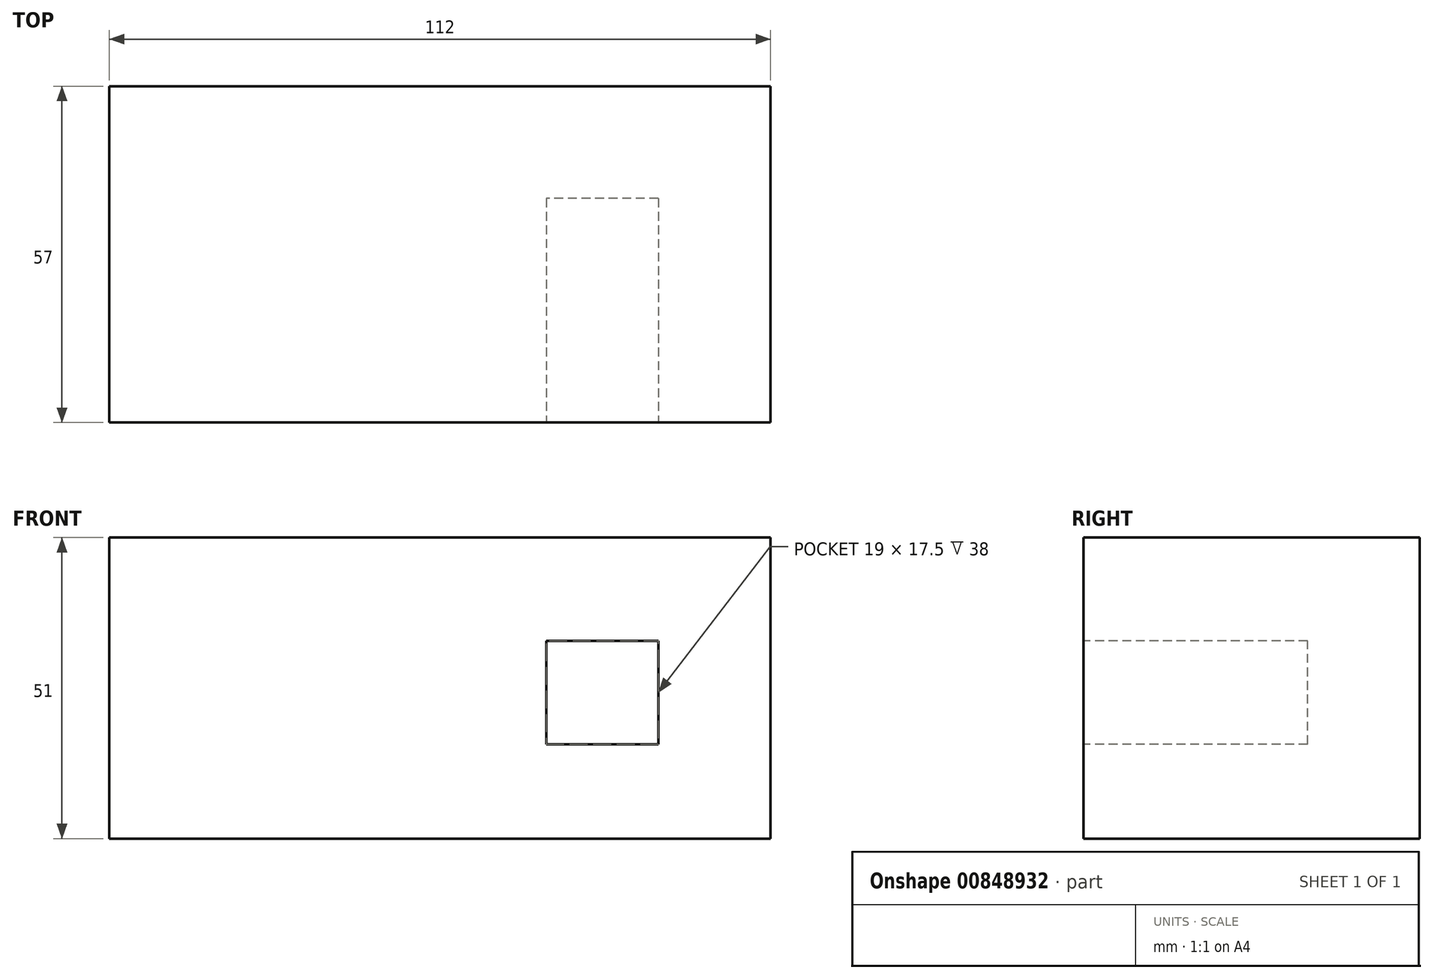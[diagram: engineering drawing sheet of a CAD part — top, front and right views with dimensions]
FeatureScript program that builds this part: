
annotation { "Feature Type Name" : "Feature", "Feature Type Description" : "" }
export const myFeature = defineFeature(function(context is Context, id is Id, definition is map)
    precondition{}
    {
        {
            var Q0;
            Q0=qCreatedBy(makeId("Front.planeOp"),FACE);
            var sketch = newSketch(context, id + "F0", { "sketchPlane" : qUnion([Q0])});
            skLineSegment(sketch, "E0.bottom", {"start": v(0, -3.04) * mm, "end": v(-112, -3.04) * mm});
            skLineSegment(sketch, "E0.top", {"start": v(0, 47.96) * mm, "end": v(-112, 47.96) * mm});
            skLineSegment(sketch, "E0.left", {"start": v(0, -3.04) * mm, "end": v(0, 47.96) * mm});
            skLineSegment(sketch, "E0.right", {"start": v(-112, -3.04) * mm, "end": v(-112, 47.96) * mm});
            skSolve(sketch);
        }
        {
            var Q0;
            Q0 = qSketchRegion(id + "F0", true);
            extrude(context, id + "F1", {"entities" : qUnion([Q0]), "depth" : 57 * mm, "offsetDistance" : 25.4 * mm});
        }
        {
            var Q0;
            Q0=makeQuery(id+"F1.opExtrude","CAP_FACE",FACE,{"disambiguationData":[OSD([sQuery(id+"F0.wireOp",EDGE,"E0.bottom"),sQuery(id+"F0.wireOp",EDGE,"E0.top"),sQuery(id+"F0.wireOp",EDGE,"E0.left"),sQuery(id+"F0.wireOp",EDGE,"E0.right")])],"isStart":false});
            var sketch = newSketch(context, id + "F2", { "sketchPlane" : qUnion([Q0])});
            skLineSegment(sketch, "E1", {"start": v(-112, -3.04) * mm, "end": v(-93, -3.04) * mm});
            skLineSegment(sketch, "E2", {"start": v(0, -3.04) * mm, "end": v(-19, -3.04) * mm});
            skLineSegment(sketch, "E3", {"start": v(-93, -3.04) * mm, "end": v(-93, 12.96) * mm});
            skLineSegment(sketch, "E4", {"start": v(-19, -3.04) * mm, "end": v(-19, 12.96) * mm});
            skLineSegment(sketch, "E5", {"start": v(-19, 12.96) * mm, "end": v(-93, 12.96) * mm});
            skLineSegment(sketch, "E6", {"start": v(-93, 47.96) * mm, "end": v(-93, 12.96) * mm});
            skLineSegment(sketch, "E7", {"start": v(-19, 12.96) * mm, "end": v(-19, 47.96) * mm});
            skLineSegment(sketch, "E8", {"start": v(-19, 47.96) * mm, "end": v(-93, 47.96) * mm});
            skLineSegment(sketch, "E9", {"start": v(-19, 12.96) * mm, "end": v(-19, 30.46) * mm});
            skLineSegment(sketch, "E10", {"start": v(-19, 30.46) * mm, "end": v(-93, 30.46) * mm});
            skLineSegment(sketch, "E11", {"start": v(-93, 30.46) * mm, "end": v(-74, 30.46) * mm});
            skLineSegment(sketch, "E12", {"start": v(-19, 30.46) * mm, "end": v(-38, 30.46) * mm});
            skLineSegment(sketch, "E13", {"start": v(-38, 30.46) * mm, "end": v(-38, 12.96) * mm});
            skLineSegment(sketch, "E14", {"start": v(-74, 30.46) * mm, "end": v(-74, 12.96) * mm});
            skSolve(sketch);
        }
        {
            var Q0;
            Q0=makeQuery(id+"F2.imprint","IMPRINT",FACE,{"disambiguationData":[TD([[makeQuery(id+"F2.imprint","IMPRINT",EDGE,{"derivedFrom":sQuery(id+"F2.wireOp",EDGE,"E7")}),1.0]])]});
            extrude(context, id + "F3", {"entities" : qUnion([Q0]), "operationType" : NewBodyOperationType.REMOVE, "oppositeDirection" : true, "depth" : 38 * mm, "offsetDistance" : 25.4 * mm});
        }
    });
